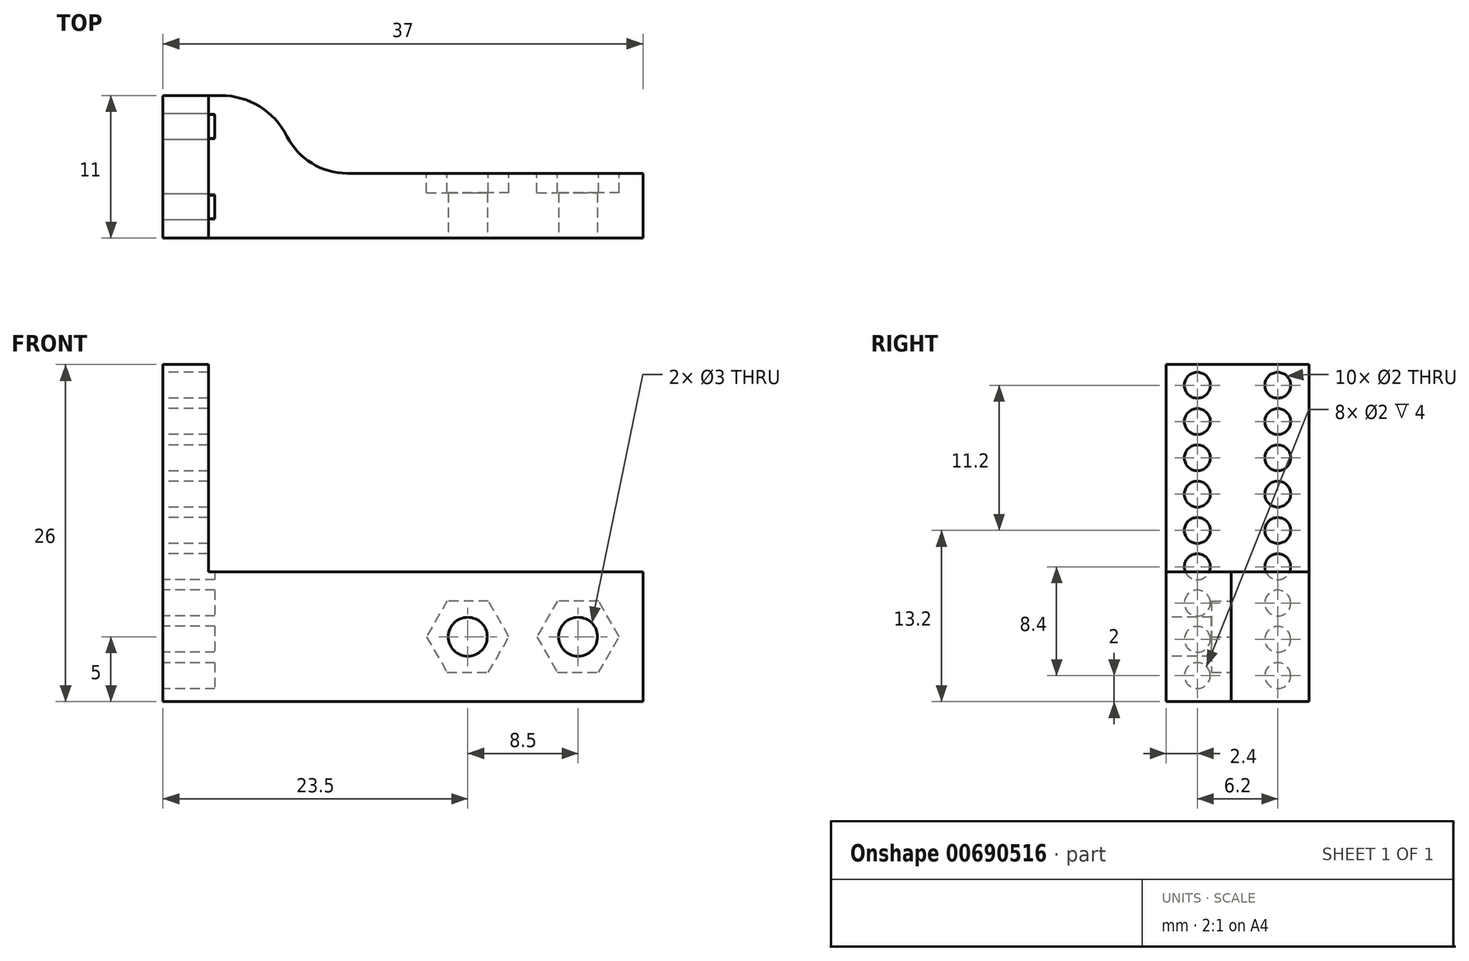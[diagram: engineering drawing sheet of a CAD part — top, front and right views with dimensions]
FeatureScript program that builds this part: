
annotation { "Feature Type Name" : "Feature", "Feature Type Description" : "" }
export const myFeature = defineFeature(function(context is Context, id is Id, definition is map)
    precondition{}
    {
        {
            var Q0;
            Q0=qCreatedBy(makeId("Front.planeOp"),FACE);
            var sketch = newSketch(context, id + "F0", { "sketchPlane" : qUnion([Q0])});
            skLineSegment(sketch, "E0", {"start": v(0, 0) * mm, "end": v(0, 10) * mm});
            skLineSegment(sketch, "E1", {"start": v(0, 10) * mm, "end": v(-37, 10) * mm});
            skLineSegment(sketch, "E2", {"start": v(-37, 0) * mm, "end": v(0, 0) * mm});
            skLineSegment(sketch, "E3", {"start": v(-37, 0) * mm, "end": v(-37, 10) * mm});
            skCircle(sketch, "E4", {"center": v(-5, 5) * mm, "radius": 1.5 * mm});
            skCircle(sketch, "E5", {"center": v(-13.5, 5) * mm, "radius": 1.5 * mm});
            skSolve(sketch);
        }
        {
            var Q0;
            Q0=makeQuery(id+"F0.imprint","IMPRINT",FACE,{"disambiguationData":[TD([[makeQuery(id+"F0.imprint","IMPRINT",EDGE,{"derivedFrom":sQuery(id+"F0.wireOp",EDGE,"E0")}),1.0]])]});
            extrude(context, id + "F1", {"entities" : qUnion([Q0]), "oppositeDirection" : true, "depth" : 11 * mm, "offsetDistance" : 25 * mm});
        }
        {
            var Q0;
            Q0=makeQuery(id+"F1.opExtrude","SWEPT_FACE",FACE,{"disambiguationData":[OSD([sQuery(id+"F0.wireOp",EDGE,"E1")])]});
            var sketch = newSketch(context, id + "F2", { "sketchPlane" : qUnion([Q0])});
            skLineSegment(sketch, "E6", {"start": v(-37, 11) * mm, "end": v(-33.5, 11) * mm});
            skLineSegment(sketch, "E7", {"start": v(-33.5, 11) * mm, "end": v(-33.5, 0) * mm});
            skLineSegment(sketch, "E8", {"start": v(-33.5, 0) * mm, "end": v(-37, 0) * mm});
            skLineSegment(sketch, "E9", {"start": v(-37, 0) * mm, "end": v(-37, 11) * mm});
            skSolve(sketch);
        }
        {
            var Q0;
            Q0=makeQuery(id+"F2.imprint","IMPRINT",FACE,{"disambiguationData":[TD([[makeQuery(id+"F2.imprint","IMPRINT",EDGE,{"derivedFrom":sQuery(id+"F2.wireOp",EDGE,"E6")}),1.0]])]});
            extrude(context, id + "F3", {"entities" : qUnion([Q0]), "operationType" : NewBodyOperationType.ADD, "depth" : 16 * mm, "offsetDistance" : 25 * mm});
        }
        {
            var Q0;
            Q0=makeQuery(id+"F3.boolean.opBoolean","MERGE",FACE,{"derivedFrom":[makeQuery(id+"F1.opExtrude","CAP_FACE",FACE,{"disambiguationData":[OSD([sQuery(id+"F0.wireOp",EDGE,"E0"),sQuery(id+"F0.wireOp",EDGE,"E1"),sQuery(id+"F0.wireOp",EDGE,"E2"),sQuery(id+"F0.wireOp",EDGE,"E3"),sQuery(id+"F0.wireOp",EDGE,"E4"),sQuery(id+"F0.wireOp",EDGE,"E5")])],"isStart":false}),makeQuery(id+"F3.opExtrude","SWEPT_FACE",FACE,{"disambiguationData":[OSD([sQuery(id+"F2.wireOp",EDGE,"E6")])]})]});
            var sketch = newSketch(context, id + "F4", { "sketchPlane" : qUnion([Q0])});
            skLineSegment(sketch, "E10", {"start": v(0, 10) * mm, "end": v(28, 10) * mm});
            skLineSegment(sketch, "E11", {"start": v(28, 10) * mm, "end": v(28, 0) * mm});
            skLineSegment(sketch, "E12", {"start": v(28, 0) * mm, "end": v(0, 0) * mm});
            skLineSegment(sketch, "E13", {"start": v(0, 0) * mm, "end": v(0, 10) * mm});
            skCircle(sketch, "E14.cCircle", {"center": v(5, 5) * mm, "radius": 2.75 * mm, "construction": true});
            skLineSegment(sketch, "E14.0", {"start": v(8.18, 5) * mm, "end": v(6.59, 2.25) * mm});
            skLineSegment(sketch, "E14.1", {"start": v(6.59, 2.25) * mm, "end": v(3.41, 2.25) * mm});
            skLineSegment(sketch, "E14.2", {"start": v(3.41, 2.25) * mm, "end": v(1.82, 5) * mm});
            skLineSegment(sketch, "E14.3", {"start": v(1.82, 5) * mm, "end": v(3.41, 7.75) * mm});
            skLineSegment(sketch, "E14.4", {"start": v(3.41, 7.75) * mm, "end": v(6.59, 7.75) * mm});
            skLineSegment(sketch, "E14.5", {"start": v(6.59, 7.75) * mm, "end": v(8.18, 5) * mm});
            skPoint(sketch, "E14.0.midPoint", {"position": v(7.38, 3.62) * mm});
            skCircle(sketch, "E15.cCircle", {"center": v(13.5, 5) * mm, "radius": 2.75 * mm, "construction": true});
            skLineSegment(sketch, "E15.0", {"start": v(15.09, 2.25) * mm, "end": v(11.91, 2.25) * mm});
            skLineSegment(sketch, "E15.1", {"start": v(11.91, 2.25) * mm, "end": v(10.32, 5) * mm});
            skLineSegment(sketch, "E15.2", {"start": v(10.32, 5) * mm, "end": v(11.91, 7.75) * mm});
            skLineSegment(sketch, "E15.3", {"start": v(11.91, 7.75) * mm, "end": v(15.09, 7.75) * mm});
            skLineSegment(sketch, "E15.4", {"start": v(15.09, 7.75) * mm, "end": v(16.68, 5) * mm});
            skLineSegment(sketch, "E15.5", {"start": v(16.68, 5) * mm, "end": v(15.09, 2.25) * mm});
            skPoint(sketch, "E15.0.midPoint", {"position": v(13.5, 2.25) * mm});
            skSolve(sketch);
        }
        {
            var Q0;
            Q0=makeQuery(id+"F4.imprint","IMPRINT",FACE,{"disambiguationData":[TD([[makeQuery(id+"F4.imprint","IMPRINT",EDGE,{"derivedFrom":sQuery(id+"F4.wireOp",EDGE,"E10")}),-1.0]])]});
            extrude(context, id + "F5", {"entities" : qUnion([Q0]), "operationType" : NewBodyOperationType.REMOVE, "oppositeDirection" : true, "depth" : 6 * mm, "offsetDistance" : 25 * mm});
        }
        {
            var Q0;
            {var subQ0=sQuery(id+"F0.wireOp",EDGE,"E4");Q0=makeQuery(id+"F5.boolean.opBoolean","SPLIT",FACE,{"disambiguationData":[TD([makeQuery(id+"F1.opExtrude","SWEPT_FACE",FACE,{"disambiguationData":[OSD([subQ0])]})])],"derivedFrom":makeQuery(id+"F3.boolean.opBoolean","MERGE",FACE,{"derivedFrom":[makeQuery(id+"F1.opExtrude","CAP_FACE",FACE,{"disambiguationData":[OSD([sQuery(id+"F0.wireOp",EDGE,"E0"),sQuery(id+"F0.wireOp",EDGE,"E1"),sQuery(id+"F0.wireOp",EDGE,"E2"),sQuery(id+"F0.wireOp",EDGE,"E3"),subQ0,sQuery(id+"F0.wireOp",EDGE,"E5")])],"isStart":false}),makeQuery(id+"F3.opExtrude","SWEPT_FACE",FACE,{"disambiguationData":[OSD([sQuery(id+"F2.wireOp",EDGE,"E6")])]})]})});}
            extrude(context, id + "F6", {"entities" : qUnion([Q0]), "operationType" : NewBodyOperationType.REMOVE, "oppositeDirection" : true, "depth" : 7.5 * mm, "offsetDistance" : 25 * mm});
        }
        {
            var Q0;
            {var subQ0=sQuery(id+"F0.wireOp",EDGE,"E5");Q0=makeQuery(id+"F5.boolean.opBoolean","SPLIT",FACE,{"disambiguationData":[TD([makeQuery(id+"F1.opExtrude","SWEPT_FACE",FACE,{"disambiguationData":[OSD([subQ0])]})])],"derivedFrom":makeQuery(id+"F3.boolean.opBoolean","MERGE",FACE,{"derivedFrom":[makeQuery(id+"F1.opExtrude","CAP_FACE",FACE,{"disambiguationData":[OSD([sQuery(id+"F0.wireOp",EDGE,"E0"),sQuery(id+"F0.wireOp",EDGE,"E1"),sQuery(id+"F0.wireOp",EDGE,"E2"),sQuery(id+"F0.wireOp",EDGE,"E3"),sQuery(id+"F0.wireOp",EDGE,"E4"),subQ0])],"isStart":false}),makeQuery(id+"F3.opExtrude","SWEPT_FACE",FACE,{"disambiguationData":[OSD([sQuery(id+"F2.wireOp",EDGE,"E6")])]})]})});}
            extrude(context, id + "F7", {"entities" : qUnion([Q0]), "operationType" : NewBodyOperationType.REMOVE, "oppositeDirection" : true, "depth" : 7.5 * mm, "offsetDistance" : 25 * mm});
        }
        {
            var Q0;
            Q0=makeQuery(id+"F3.boolean.opBoolean","MERGE",FACE,{"derivedFrom":[makeQuery(id+"F1.opExtrude","SWEPT_FACE",FACE,{"disambiguationData":[OSD([sQuery(id+"F0.wireOp",EDGE,"E3")])]}),makeQuery(id+"F3.opExtrude","SWEPT_FACE",FACE,{"disambiguationData":[OSD([sQuery(id+"F2.wireOp",EDGE,"E9")])]})]});
            var sketch = newSketch(context, id + "F8", { "sketchPlane" : qUnion([Q0])});
            skCircle(sketch, "E16", {"center": v(-8.6, 2) * mm, "radius": 1 * mm});
            skCircle(sketch, "E17", {"center": v(-2.4, 2) * mm, "radius": 1 * mm});
            skCircle(sketch, "E18.1.0.0", {"center": v(-2.4, 4.8) * mm, "radius": 1 * mm});
            skCircle(sketch, "E18.1.0.1", {"center": v(-8.6, 4.8) * mm, "radius": 1 * mm});
            skCircle(sketch, "E18.2.0.0", {"center": v(-2.4, 7.6) * mm, "radius": 1 * mm});
            skCircle(sketch, "E18.2.0.1", {"center": v(-8.6, 7.6) * mm, "radius": 1 * mm});
            skCircle(sketch, "E18.3.0.0", {"center": v(-2.4, 10.4) * mm, "radius": 1 * mm});
            skCircle(sketch, "E18.3.0.1", {"center": v(-8.6, 10.4) * mm, "radius": 1 * mm});
            skCircle(sketch, "E18.4.0.0", {"center": v(-2.4, 13.2) * mm, "radius": 1 * mm});
            skCircle(sketch, "E18.4.0.1", {"center": v(-8.6, 13.2) * mm, "radius": 1 * mm});
            skCircle(sketch, "E18.5.0.0", {"center": v(-2.4, 16) * mm, "radius": 1 * mm});
            skCircle(sketch, "E18.5.0.1", {"center": v(-8.6, 16) * mm, "radius": 1 * mm});
            skCircle(sketch, "E18.6.0.0", {"center": v(-2.4, 18.8) * mm, "radius": 1 * mm});
            skCircle(sketch, "E18.6.0.1", {"center": v(-8.6, 18.8) * mm, "radius": 1 * mm});
            skCircle(sketch, "E18.7.0.0", {"center": v(-2.4, 21.6) * mm, "radius": 1 * mm});
            skCircle(sketch, "E18.7.0.1", {"center": v(-8.6, 21.6) * mm, "radius": 1 * mm});
            skCircle(sketch, "E18.8.0.0", {"center": v(-2.4, 24.4) * mm, "radius": 1 * mm});
            skCircle(sketch, "E18.8.0.1", {"center": v(-8.6, 24.4) * mm, "radius": 1 * mm});
            skLineSegment(sketch, "E18.direction1", {"start": v(-8.6, 2) * mm, "end": v(-8.6, 4.8) * mm, "construction": true});
            skSolve(sketch);
        }
        {
            var Q0;
            Q0 = qSketchRegion(id + "F8", true);
            extrude(context, id + "F9", {"entities" : qUnion([Q0]), "operationType" : NewBodyOperationType.REMOVE, "oppositeDirection" : true, "depth" : 4 * mm, "offsetDistance" : 25 * mm});
        }
        {
            var Q0;
            Q0=makeQuery(id+"F5.boolean.opBoolean","COPY",EDGE,{"derivedFrom":makeQuery(id+"F5.opExtrude","CAP_EDGE",EDGE,{"disambiguationData":[OSD([sQuery(id+"F4.wireOp",EDGE,"E11")])],"isStart":false})});
            fillet(context, id + "F10", {"entities" : qUnion([Q0]), "radius" : 5.2 * mm, "tangentPropagation" : true, "allowEdgeOverflow" : false});
        }
        {
            var Q0;
            Q0=makeQuery(id+"F5.boolean.opBoolean","COPY",EDGE,{"derivedFrom":makeQuery(id+"F5.opExtrude","CAP_EDGE",EDGE,{"disambiguationData":[OSD([sQuery(id+"F4.wireOp",EDGE,"E11")])],"isStart":true})});
            fillet(context, id + "F11", {"entities" : qUnion([Q0]), "radius" : 5.7 * mm, "tangentPropagation" : true, "allowEdgeOverflow" : false});
        }
    });
